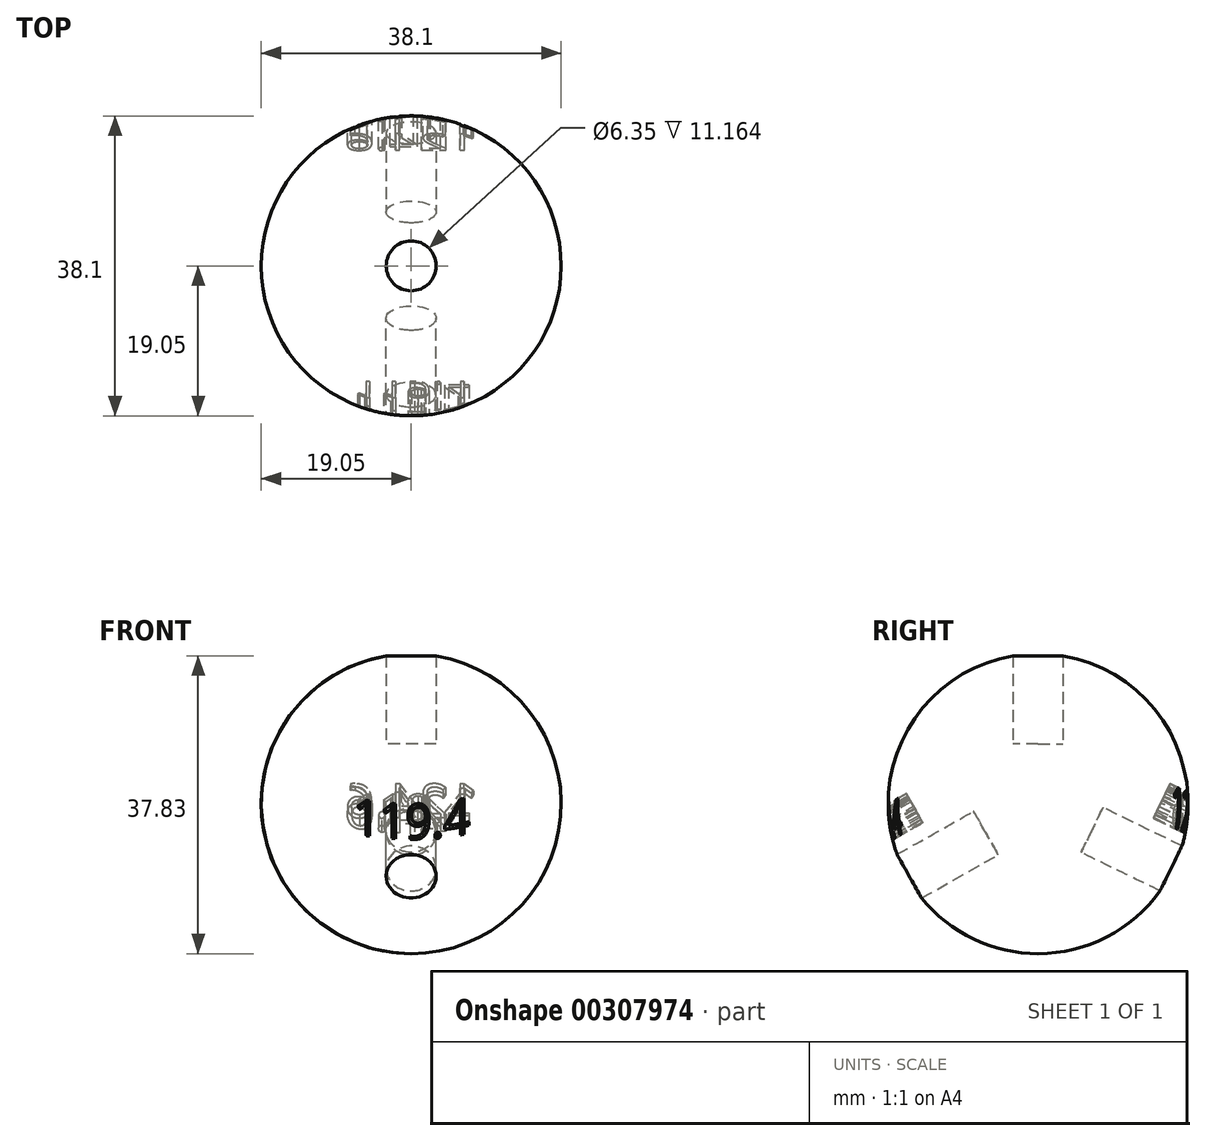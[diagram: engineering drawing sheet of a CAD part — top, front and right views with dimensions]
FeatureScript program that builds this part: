
annotation { "Feature Type Name" : "Feature", "Feature Type Description" : "" }
export const myFeature = defineFeature(function(context is Context, id is Id, definition is map)
    precondition{}
    {
        {
            var Q0;
            Q0=qCreatedBy(makeId("Front.planeOp"),FACE);
            var sketch = newSketch(context, id + "F0", { "sketchPlane" : qUnion([Q0])});
            skArc(sketch, "E0", {"start": v(0, 19.05) * mm, "mid": v(-19.05, 0) * mm, "end": v(0, -19.05) * mm});
            skLineSegment(sketch, "E1", {"start": v(0, 19.05) * mm, "end": v(0, -19.05) * mm});
            skSolve(sketch);
        }
        {
            var Q0;
            Q0=qCreatedBy(makeId("Top.planeOp"),FACE);
            var sketch = newSketch(context, id + "F1", { "sketchPlane" : qUnion([Q0])});
            skCircle(sketch, "E2", {"center": v(0, 0) * mm, "radius": 19.05 * mm});
            skSolve(sketch);
        }
        {
            var Q0;
            Q0=makeQuery(id+"F0.imprint","IMPRINT",FACE,{"disambiguationData":[TD([[makeQuery(id+"F0.imprint","IMPRINT",EDGE,{"derivedFrom":sQuery(id+"F0.wireOp",EDGE,"E0")}),1.0]])]});
            var Q1;
            Q1=sQuery(id+"F1.wireOp",EDGE,"E2");
            revolve(context, id + "F2", {"entities" : qUnion([Q0]), "axis" : qUnion([Q1]), "revolveType" : RevolveType.FULL});
        }
        {
            var Q0;
            Q0=qCreatedBy(makeId("Front.planeOp"),FACE);
            var sketch = newSketch(context, id + "F3", { "sketchPlane" : qUnion([Q0])});
            skLineSegment(sketch, "E3", {"start": v(0, 0) * mm, "end": v(76.32, 0) * mm, "construction": true});
            skLineSegment(sketch, "E4", {"start": v(0, 0) * mm, "end": v(0, 76.7) * mm, "construction": true});
            skSolve(sketch);
        }
        {
            var Q0;
            Q0=qCreatedBy(makeId("Top.planeOp"),FACE);
            cPlane(context, id + "F4", {"entities" : qUnion([Q0]), "cplaneType" : CPlaneType.OFFSET, "offset" : 7.62 * mm, "width" : 152.4 * mm, "height" : 152.4 * mm});
        }
        {
            var Q0;
            Q0=qCreatedBy(id+"F4.planeOp",FACE);
            var sketch = newSketch(context, id + "F5", { "sketchPlane" : qUnion([Q0])});
            skCircle(sketch, "E5", {"center": v(0, 0) * mm, "radius": 3.17 * mm});
            skSolve(sketch);
        }
        {
            var Q0;
            Q0=qSketchRegion(id+"F5",true);
            extrude(context, id + "F6", {"entities" : qUnion([Q0]), "depth" : 76.2 * mm});
        }
        {
            var Q0;
            Q0=makeQuery(id+"F6.opExtrude","SWEPT_BODY",BODY,{"disambiguationData":[OSD([sQuery(id+"F5.wireOp",EDGE,"E5")])]});
            var Q1;
            Q1=sQuery(id+"F3.wireOp",EDGE,"E3");
            transform(context, id + "F7", {"entities" : qUnion([Q0]), "transformType" : TransformType.ROTATION, "transformAxis" : qUnion([Q1]), "angle" : 119.4 * degree, "makeCopy" : true});
        }
        {
            var Q0;
            Q0=makeQuery(id+"F7.opPattern","COPY",BODY,{"derivedFrom":makeQuery(id+"F6.opExtrude","SWEPT_BODY",BODY,{"disambiguationData":[OSD([sQuery(id+"F5.wireOp",EDGE,"E5")])]}),"instanceName":"1"});
            var Q1;
            Q1=sQuery(id+"F3.wireOp",EDGE,"E3");
            transform(context, id + "F8", {"entities" : qUnion([Q0]), "transformType" : TransformType.ROTATION, "transformAxis" : qUnion([Q1]), "angle" : 124.6 * degree, "makeCopy" : true});
        }
        {
            var Q0;
            Q0=makeQuery(id+"F7.opPattern","COPY",FACE,{"derivedFrom":makeQuery(id+"F6.opExtrude","CAP_FACE",FACE,{"disambiguationData":[OSD([sQuery(id+"F5.wireOp",EDGE,"E5")])],"isStart":false}),"instanceName":"1"});
            cPlane(context, id + "F9", {"entities" : qUnion([Q0]), "cplaneType" : CPlaneType.OFFSET, "offset" : 63.5 * mm, "oppositeDirection" : true, "width" : 152.4 * mm, "height" : 152.4 * mm});
        }
        {
            var Q0;
            Q0=qCreatedBy(id+"F9.planeOp",FACE);
            var sketch = newSketch(context, id + "F10", { "sketchPlane" : qUnion([Q0])});
            skText(sketch, "E6", { "text": "119.4", "fontName": "OpenSans-Regular.ttf"});
            const initialGuessF10  = {"E6": [-0.00732, 0.00517, 1, 0, 0.00416]};
            skSetInitialGuess(sketch, initialGuessF10);
            skSolve(sketch);
        }
        {
            var Q0;
            Q0=qSketchRegion(id+"F10",true);
            extrude(context, id + "F11", {"entities" : qUnion([Q0]), "operationType" : NewBodyOperationType.REMOVE, "oppositeDirection" : true, "depth" : 6.35 * mm});
        }
        {
            var Q0;
            Q0=makeQuery(id+"F8.opPattern","COPY",FACE,{"derivedFrom":makeQuery(id+"F7.opPattern","COPY",FACE,{"derivedFrom":makeQuery(id+"F6.opExtrude","CAP_FACE",FACE,{"disambiguationData":[OSD([sQuery(id+"F5.wireOp",EDGE,"E5")])],"isStart":false}),"instanceName":"1"}),"instanceName":"1"});
            cPlane(context, id + "F12", {"entities" : qUnion([Q0]), "cplaneType" : CPlaneType.OFFSET, "offset" : 63.5 * mm, "oppositeDirection" : true, "width" : 152.4 * mm, "height" : 152.4 * mm});
        }
        {
            var Q0;
            Q0=qCreatedBy(id+"F12.planeOp",FACE);
            var sketch = newSketch(context, id + "F13", { "sketchPlane" : qUnion([Q0])});
            skText(sketch, "E7", { "text": "124.6", "fontName": "OpenSans-Regular.ttf"});
            const initialGuessF13  = {"E7": [-0.00854, 0.00485, 1, 0, 0.00478]};
            skSetInitialGuess(sketch, initialGuessF13);
            skSolve(sketch);
        }
        {
            var Q0;
            Q0=qSketchRegion(id+"F13",true);
            extrude(context, id + "F14", {"entities" : qUnion([Q0]), "operationType" : NewBodyOperationType.REMOVE, "oppositeDirection" : true, "depth" : 6.35 * mm});
        }
        {
            var Q0;
            Q0=makeQuery(id+"F6.opExtrude","SWEPT_BODY",BODY,{"disambiguationData":[OSD([sQuery(id+"F5.wireOp",EDGE,"E5")])]});
            var Q1;
            Q1=makeQuery(id+"F8.opPattern","COPY",BODY,{"derivedFrom":makeQuery(id+"F7.opPattern","COPY",BODY,{"derivedFrom":makeQuery(id+"F6.opExtrude","SWEPT_BODY",BODY,{"disambiguationData":[OSD([sQuery(id+"F5.wireOp",EDGE,"E5")])]}),"instanceName":"1"}),"instanceName":"1"});
            var Q2;
            Q2=makeQuery(id+"F7.opPattern","COPY",BODY,{"derivedFrom":makeQuery(id+"F6.opExtrude","SWEPT_BODY",BODY,{"disambiguationData":[OSD([sQuery(id+"F5.wireOp",EDGE,"E5")])]}),"instanceName":"1"});
            var Q3;
            Q3=makeQuery(id+"F2.opRevolve","SWEPT_BODY",BODY,{"disambiguationData":[OSD([sQuery(id+"F0.wireOp",EDGE,"E0"),sQuery(id+"F0.wireOp",EDGE,"E1")])]});
            booleanBodies(context, id + "F15", {"operationType" : BooleanOperationType.SUBTRACTION, "tools" : qUnion([Q0, Q1, Q2]), "targets" : qUnion([Q3])});
        }
    });
